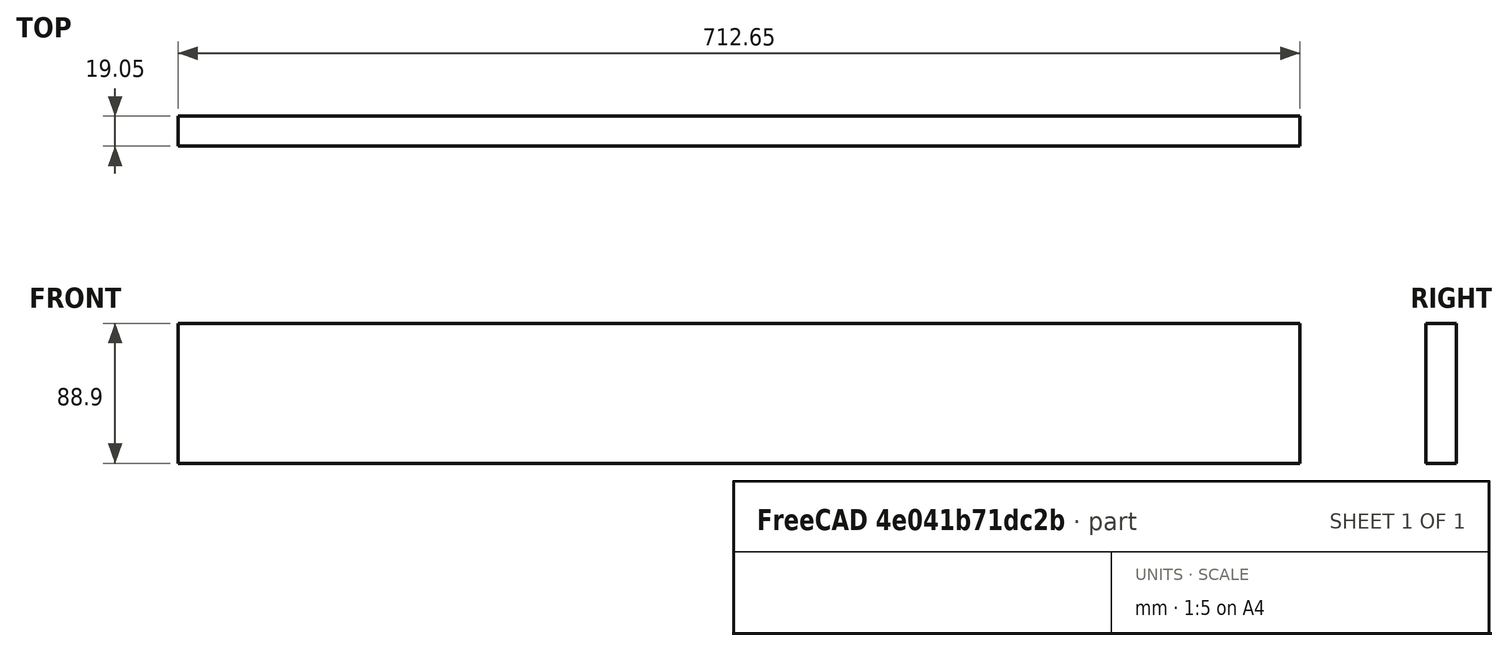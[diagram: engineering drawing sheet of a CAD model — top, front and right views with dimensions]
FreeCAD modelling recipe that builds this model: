
FCSTD DOCUMENT  (FreeCAD 0.19R24291 (Git))
Label: frontFoot
License: All rights reserved
LicenseURL: http://en.wikipedia.org/wiki/All_rights_reserved
objects: Sketcher::SketchObject×2, PartDesign::Pad×1, PartDesign::Body×1
note: 5 computed .brp shape members not serialized (recipe doc carries the construction recipe); baked Part::Feature solids carry a one-line shape summary decoded from their .brp

FEATURE [Sketcher::SketchObject] Sketch
  FullyConstrained = true
  MapMode = 5
  Placement = pos=(0,0,0) rot=(0.57735,0.57735,0.57735;2.0944rad)
  Support = -> [YZ_Plane]
  expr: Constraints[9] = 3.5 * 25.4
  sketch-geometry (4):
    g0: LineSegment StartX=0 StartY=0 StartZ=0 EndX=19.05 EndY=0 EndZ=0
    g1: LineSegment StartX=19.05 StartY=0 StartZ=0 EndX=19.05 EndY=88.9 EndZ=0
    g2: LineSegment StartX=19.05 StartY=88.9 StartZ=0 EndX=0 EndY=88.9 EndZ=0
    g3: LineSegment StartX=0 StartY=88.9 StartZ=0 EndX=0 EndY=0 EndZ=0
  constraints (11):
    c: Coincident(g0,g1)
    c: Coincident(g1,g2)
    c: Coincident(g2,g3)
    c: Coincident(g3,g0)
    c: Horizontal(g0)
    c: Horizontal(g2)
    c: Vertical(g1)
    c: Vertical(g3)
    c: Coincident(g0,g-1)
    c: DistanceY(g3,g3) = 88.9
    c: DistanceX(g0,g0) = 19.05
FEATURE [PartDesign::Pad] Pad
  Direction = (1,1,1)
  Length = 712.65
  Length2 = 100
  Placement = pos=(0,0,0) rot=(0.57735,0.57735,0.57735;2.0944rad)
  Profile = -> Sketch
  Type = 0
FEATURE [Sketcher::SketchObject] Sketch001
  FullyConstrained = true
  MapMode = 5
  Support = -> [XY_Plane]
  expr: Constraints[104] = 3 / 4 / 2 * 25.4
  expr: Constraints[72] = 3 / 4 * 25.4
  expr: Constraints[67] = 3.5 * 25.4
  expr: Constraints[45] = (3.5 / 2 - 3 / 4 / 2) * 25.4
  expr: Constraints[32] = (3.5 / 2 - 3 / 4 / 2) * 25.4
  expr: Constraints[17] = 3.5 * 25.4
  expr: Constraints[28] = 3 / 4 * 25.4
  expr: Constraints[44] = 3 / 4 * 25.4
  expr: Constraints[8] = 3 / 4 * 25.4
  sketch-geometry (41):
    g0: LineSegment StartX=0 StartY=631.05 StartZ=0 EndX=19.05 EndY=631.05 EndZ=0
    g1: LineSegment StartX=19.05 StartY=631.05 StartZ=0 EndX=19.05 EndY=0 EndZ=0
    g2: LineSegment StartX=19.05 StartY=0 StartZ=0 EndX=0 EndY=0 EndZ=0
    g3: LineSegment StartX=0 StartY=0 StartZ=0 EndX=0 EndY=631.05 EndZ=0
    g4: LineSegment StartX=19.05 StartY=88.9 StartZ=0 EndX=763.45 EndY=88.9 EndZ=0
    g5: LineSegment StartX=763.45 StartY=88.9 StartZ=0 EndX=763.45 EndY=0 EndZ=0
    g6: LineSegment StartX=763.45 StartY=0 StartZ=0 EndX=19.05 EndY=0 EndZ=0
    g7: LineSegment StartX=19.05 StartY=0 StartZ=0 EndX=19.05 EndY=88.9 EndZ=0
    g8: LineSegment StartX=34.925 StartY=53.975 StartZ=0 EndX=747.575 EndY=53.975 EndZ=0
    g9: LineSegment StartX=747.575 StartY=53.975 StartZ=0 EndX=747.575 EndY=34.925 EndZ=0
    g10: LineSegment StartX=747.575 StartY=34.925 StartZ=0 EndX=34.925 EndY=34.925 EndZ=0
    g11: LineSegment StartX=34.925 StartY=34.925 StartZ=0 EndX=34.925 EndY=53.975 EndZ=0
    g12: LineSegment StartX=34.925 StartY=44.45 StartZ=0 EndX=747.575 EndY=44.45 EndZ=0
    g13: GeomPoint X=19.05 Y=44.45 Z=0
    g14: LineSegment StartX=763.45 StartY=0 StartZ=0 EndX=782.5 EndY=0 EndZ=0
    g15: LineSegment StartX=782.5 StartY=0 StartZ=0 EndX=782.5 EndY=631.05 EndZ=0
    g16: LineSegment StartX=782.5 StartY=631.05 StartZ=0 EndX=763.45 EndY=631.05 EndZ=0
    g17: LineSegment StartX=763.45 StartY=631.05 StartZ=0 EndX=763.45 EndY=0 EndZ=0
    g18: LineSegment StartX=34.925 StartY=577.075 StartZ=0 EndX=53.975 EndY=577.075 EndZ=0
    g19: LineSegment StartX=53.975 StartY=577.075 StartZ=0 EndX=53.975 EndY=53.975 EndZ=0
    g20: LineSegment StartX=53.975 StartY=53.975 StartZ=0 EndX=34.925 EndY=53.975 EndZ=0
    g21: LineSegment StartX=34.925 StartY=53.975 StartZ=0 EndX=34.925 EndY=577.075 EndZ=0
    g22: LineSegment StartX=19.05 StartY=631.05 StartZ=0 EndX=763.45 EndY=631.05 EndZ=0
    g23: LineSegment StartX=763.45 StartY=631.05 StartZ=0 EndX=763.45 EndY=542.15 EndZ=0
    g24: LineSegment StartX=763.45 StartY=542.15 StartZ=0 EndX=19.05 EndY=542.15 EndZ=0
    g25: LineSegment StartX=19.05 StartY=542.15 StartZ=0 EndX=19.05 EndY=631.05 EndZ=0
    g26: LineSegment StartX=19.05 StartY=586.6 StartZ=0 EndX=763.45 EndY=586.6 EndZ=0
    g27: LineSegment StartX=53.975 StartY=88.9 StartZ=0 EndX=88.9 EndY=88.9 EndZ=0
    g28: LineSegment StartX=88.9 StartY=88.9 StartZ=0 EndX=88.9 EndY=53.975 EndZ=0
    g29: LineSegment StartX=88.9 StartY=53.975 StartZ=0 EndX=53.975 EndY=53.975 EndZ=0
    g30: LineSegment StartX=53.975 StartY=53.975 StartZ=0 EndX=53.975 EndY=88.9 EndZ=0
    g31: LineSegment StartX=53.975 StartY=88.9 StartZ=0 EndX=88.9 EndY=53.975 EndZ=0
    g32: LineSegment StartX=88.9 StartY=88.9 StartZ=0 EndX=53.975 EndY=53.975 EndZ=0
    g33: Circle CenterX=71.4375 CenterY=71.4375 CenterZ=0 NormalX=0 NormalY=0 NormalZ=1 AngleXU=0 Radius=3.42
    g34: LineSegment StartX=53.975 StartY=577.075 StartZ=0 EndX=88.9 EndY=577.075 EndZ=0
    g35: LineSegment StartX=88.9 StartY=577.075 StartZ=0 EndX=88.9 EndY=542.15 EndZ=0
    g36: LineSegment StartX=88.9 StartY=542.15 StartZ=0 EndX=53.975 EndY=542.15 EndZ=0
    g37: LineSegment StartX=53.975 StartY=542.15 StartZ=0 EndX=53.975 EndY=577.075 EndZ=0
    g38: LineSegment StartX=53.975 StartY=577.075 StartZ=0 EndX=88.9 EndY=542.15 EndZ=0
    g39: LineSegment StartX=88.9 StartY=577.075 StartZ=0 EndX=53.975 EndY=542.15 EndZ=0
    g40: Circle CenterX=71.4375 CenterY=559.612 CenterZ=0 NormalX=0 NormalY=0 NormalZ=1 AngleXU=0 Radius=3.14
  constraints (117):
    c: Coincident(g0,g1)
    c: Coincident(g1,g2)
    c: Coincident(g2,g3)
    c: Coincident(g3,g0)
    c: Horizontal(g0)
    c: Horizontal(g2)
    c: Vertical(g1)
    c: Vertical(g3)
    c: DistanceX(g2,g2) = 19.05
    c: Coincident(g4,g5)
    c: Coincident(g5,g6)
    c: Coincident(g6,g7)
    c: Coincident(g7,g4)
    c: Horizontal(g4)
    c: Horizontal(g6)
    c: Vertical(g5)
    c: Vertical(g7)
    c: DistanceY(g7,g7) = 88.9
    c: DistanceX(g6,g6) = 744.4
    c: Coincident(g1,g6)
    c: Coincident(g8,g9)
    c: Coincident(g9,g10)
    c: Coincident(g10,g11)
    c: Coincident(g11,g8)
    c: Horizontal(g8)
    c: Horizontal(g10)
    c: Vertical(g9)
    c: Vertical(g11)
    c: DistanceY(g11,g11) = 19.05
    c: Horizontal(g12)
    c: Symmetric(g10,g8,g12)
    c: PointOnObject(g12,g9)
    c: DistanceX(g2,g10) = 34.925
    c: Symmetric(g1,g4,g13)
    c: Horizontal(g12,g13)
    c: Coincident(g14,g15)
    c: Coincident(g15,g16)
    c: Coincident(g16,g17)
    c: Coincident(g17,g14)
    c: Horizontal(g14)
    c: Horizontal(g16)
    c: Vertical(g15)
    c: Vertical(g17)
    c: Coincident(g14,g5)
    c: DistanceX(g14,g14) = 19.05
    c: DistanceX(g9,g14) = 34.925
    c: DistanceX(g10,g10) = 712.65
    c: Coincident(g18,g19)
    c: Coincident(g19,g20)
    c: Coincident(g20,g21)
    c: Coincident(g21,g18)
    c: Horizontal(g18)
    c: Horizontal(g20)
    c: Vertical(g19)
    c: Vertical(g21)
    c: DistanceY(g3,g3) = 631.05
    c: DistanceY(g15,g15) = 631.05
    c: Coincident(g22,g23)
    c: Coincident(g23,g24)
    c: Coincident(g24,g25)
    c: Coincident(g25,g22)
    c: Horizontal(g22)
    c: Horizontal(g24)
    c: Vertical(g23)
    c: Vertical(g25)
    c: Coincident(g22,g0)
    c: PointOnObject(g23,g17)
    c: DistanceY(g25,g25) = 88.9
    c: Horizontal(g26)
    c: Symmetric(g24,g0,g26)
    c: PointOnObject(g26,g17)
    c: Coincident(g20,g8)
    c: DistanceX(g18,g18) = 19.05
    c: DistanceY(g19,g19) = 523.1
    c: Coincident(g27,g28)
    c: Coincident(g28,g29)
    c: Coincident(g29,g30)
    c: Coincident(g30,g27)
    c: Horizontal(g27)
    c: Horizontal(g29)
    c: Vertical(g28)
    c: Vertical(g30)
    c: Coincident(g29,g19)
    c: Equal(g27,g28)
    c: PointOnObject(g27,g4)
    c: DistanceX(g27,g27) = 34.925
    c: Coincident(g31,g27)
    c: Coincident(g31,g28)
    c: Coincident(g32,g27)
    c: Coincident(g32,g19)
    c: PointOnObject(g33,g31)
    c: PointOnObject(g33,g32)
    c: DistanceX(g4,g33) = 52.3875
    c: DistanceY(g33,g4) = 17.4625
    c: Coincident(g34,g35)
    c: Coincident(g35,g36)
    c: Coincident(g36,g37)
    c: Coincident(g37,g34)
    c: Horizontal(g34)
    c: Horizontal(g36)
    c: Vertical(g35)
    c: Vertical(g37)
    c: Equal(g36,g27)
    c: Equal(g35,g34)
    c: DistanceY(g18,g26) = 9.525
    c: Coincident(g34,g18)
    c: Coincident(g38,g18)
    c: Coincident(g38,g35)
    c: Coincident(g39,g34)
    c: Coincident(g39,g36)
    c: PointOnObject(g40,g39)
    c: PointOnObject(g40,g38)
    c: DistanceX(g24,g40) = 52.3875
    c: DistanceY(g24,g40) = 17.4625
    c: Diameter(g40) = 6.28
    c: Coincident(g-1,g2)
    c: Diameter(g33) = 6.84
FEATURE [PartDesign::Body] Body
  Group = -> [Sketch,Pad,Sketch001]
  Origin = -> Origin
  Tip = -> Pad
